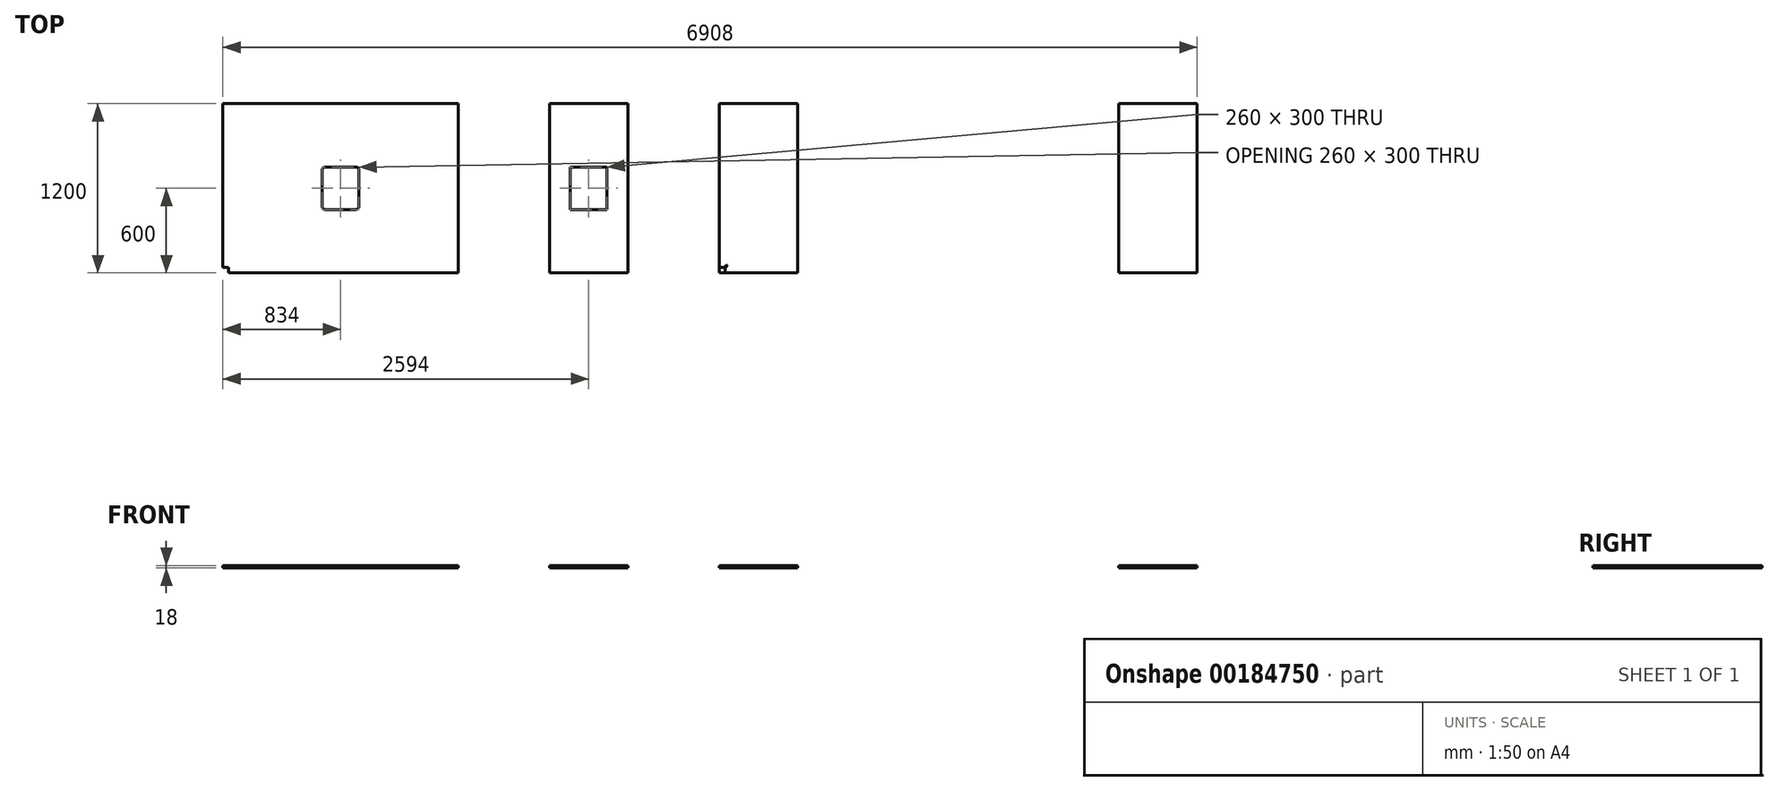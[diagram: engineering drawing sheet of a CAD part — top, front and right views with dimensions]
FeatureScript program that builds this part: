
annotation { "Feature Type Name" : "Feature", "Feature Type Description" : "" }
export const myFeature = defineFeature(function(context is Context, id is Id, definition is map)
    precondition{}
    {
        {
            var Q0;
            Q0=qCreatedBy(makeId("Top.planeOp"),FACE);
            var sketch = newSketch(context, id + "F0", { "sketchPlane" : qUnion([Q0])});
            skLineSegment(sketch, "E0.bottom", {"start": v(834, 600) * mm, "end": v(-834, 600) * mm});
            skLineSegment(sketch, "E0.top", {"start": v(834, -600) * mm, "end": v(-834, -600) * mm});
            skLineSegment(sketch, "E0.left", {"start": v(834, 600) * mm, "end": v(834, -600) * mm});
            skLineSegment(sketch, "E0.right", {"start": v(-834, 600) * mm, "end": v(-834, -600) * mm});
            skPoint(sketch, "E0.middle", {"position": v(0, 0) * mm});
            skLineSegment(sketch, "E1.bottom", {"start": v(130, 150) * mm, "end": v(-130, 150) * mm});
            skLineSegment(sketch, "E1.top", {"start": v(130, -150) * mm, "end": v(-130, -150) * mm});
            skLineSegment(sketch, "E1.left", {"start": v(130, 150) * mm, "end": v(130, -150) * mm});
            skLineSegment(sketch, "E1.right", {"start": v(-130, 150) * mm, "end": v(-130, -150) * mm});
            skLineSegment(sketch, "E2.bottom", {"start": v(-834, -600) * mm, "end": v(-794, -600) * mm});
            skLineSegment(sketch, "E2.top", {"start": v(-834, -560) * mm, "end": v(-794, -560) * mm});
            skLineSegment(sketch, "E2.left", {"start": v(-834, -600) * mm, "end": v(-834, -560) * mm});
            skLineSegment(sketch, "E2.right", {"start": v(-794, -600) * mm, "end": v(-794, -560) * mm});
            skSolve(sketch);
        }
        {
            var Q0;
            Q0=makeQuery(id+"F0.imprint","IMPRINT",FACE,{"disambiguationData":[TD([[makeQuery(id+"F0.imprint","IMPRINT",EDGE,{"derivedFrom":sQuery(id+"F0.wireOp",EDGE,"E0.bottom")}),1.0]])]});
            extrude(context, id + "F1", {"entities" : qUnion([Q0]), "depth" : 18 * mm});
        }
        {
            var Q0;
            Q0=makeQuery(id+"F1.opExtrude","SWEPT_BODY",BODY,{"disambiguationData":[OSD([sQuery(id+"F0.wireOp",EDGE,"E0.bottom"),sQuery(id+"F0.wireOp",EDGE,"E0.top"),sQuery(id+"F0.wireOp",EDGE,"E0.left"),sQuery(id+"F0.wireOp",EDGE,"E0.right"),sQuery(id+"F0.wireOp",EDGE,"E1.bottom"),sQuery(id+"F0.wireOp",EDGE,"E1.top"),sQuery(id+"F0.wireOp",EDGE,"E1.left"),sQuery(id+"F0.wireOp",EDGE,"E1.right"),sQuery(id+"F0.wireOp",EDGE,"E2.top"),sQuery(id+"F0.wireOp",EDGE,"E2.right")])]});
            transform(context, id + "F2", {"entities" : qUnion([Q0]), "transformType" : TransformType.TRANSLATION_3D, "dx" : 1760 * mm, "dy" : 0 * mm, "dz" : 0 * mm, "makeCopy" : true});
        }
        {
            var Q0;
            Q0=makeQuery(id+"F2.opPattern","COPY",BODY,{"derivedFrom":makeQuery(id+"F1.opExtrude","SWEPT_BODY",BODY,{"disambiguationData":[OSD([sQuery(id+"F0.wireOp",EDGE,"E0.bottom"),sQuery(id+"F0.wireOp",EDGE,"E0.top"),sQuery(id+"F0.wireOp",EDGE,"E0.left"),sQuery(id+"F0.wireOp",EDGE,"E0.right"),sQuery(id+"F0.wireOp",EDGE,"E1.bottom"),sQuery(id+"F0.wireOp",EDGE,"E1.top"),sQuery(id+"F0.wireOp",EDGE,"E1.left"),sQuery(id+"F0.wireOp",EDGE,"E1.right"),sQuery(id+"F0.wireOp",EDGE,"E2.top"),sQuery(id+"F0.wireOp",EDGE,"E2.right")])]}),"instanceName":"1"});
            transform(context, id + "F3", {"entities" : qUnion([Q0]), "transformType" : TransformType.TRANSLATION_3D, "dx" : 1760 * mm, "dy" : 0 * mm, "dz" : 0 * mm, "makeCopy" : true});
        }
        {
            var Q0;
            Q0=makeQuery(id+"F3.opPattern","COPY",BODY,{"derivedFrom":makeQuery(id+"F2.opPattern","COPY",BODY,{"derivedFrom":makeQuery(id+"F1.opExtrude","SWEPT_BODY",BODY,{"disambiguationData":[OSD([sQuery(id+"F0.wireOp",EDGE,"E0.bottom"),sQuery(id+"F0.wireOp",EDGE,"E0.top"),sQuery(id+"F0.wireOp",EDGE,"E0.left"),sQuery(id+"F0.wireOp",EDGE,"E0.right"),sQuery(id+"F0.wireOp",EDGE,"E1.bottom"),sQuery(id+"F0.wireOp",EDGE,"E1.top"),sQuery(id+"F0.wireOp",EDGE,"E1.left"),sQuery(id+"F0.wireOp",EDGE,"E1.right"),sQuery(id+"F0.wireOp",EDGE,"E2.top"),sQuery(id+"F0.wireOp",EDGE,"E2.right")])]}),"instanceName":"1"}),"instanceName":"1"});
            transform(context, id + "F4", {"entities" : qUnion([Q0]), "transformType" : TransformType.TRANSLATION_3D, "dx" : 1720 * mm, "dy" : 0 * mm, "dz" : 0 * mm, "makeCopy" : true});
        }
        {
            var Q0;
            Q0=makeQuery(id+"F2.opPattern","COPY",FACE,{"derivedFrom":makeQuery(id+"F1.opExtrude","CAP_FACE",FACE,{"disambiguationData":[OSD([sQuery(id+"F0.wireOp",EDGE,"E0.bottom"),sQuery(id+"F0.wireOp",EDGE,"E0.top"),sQuery(id+"F0.wireOp",EDGE,"E0.left"),sQuery(id+"F0.wireOp",EDGE,"E0.right"),sQuery(id+"F0.wireOp",EDGE,"E1.bottom"),sQuery(id+"F0.wireOp",EDGE,"E1.top"),sQuery(id+"F0.wireOp",EDGE,"E1.left"),sQuery(id+"F0.wireOp",EDGE,"E1.right"),sQuery(id+"F0.wireOp",EDGE,"E2.top"),sQuery(id+"F0.wireOp",EDGE,"E2.right")])],"isStart":false}),"instanceName":"1"});
            var sketch = newSketch(context, id + "F5", { "sketchPlane" : qUnion([Q0])});
            skLineSegment(sketch, "E3.bottom", {"start": v(926, 600) * mm, "end": v(1482, 600) * mm});
            skLineSegment(sketch, "E3.top", {"start": v(926, -600) * mm, "end": v(1482, -600) * mm});
            skLineSegment(sketch, "E3.left", {"start": v(926, 600) * mm, "end": v(926, -600) * mm});
            skLineSegment(sketch, "E3.right", {"start": v(1482, 600) * mm, "end": v(1482, -600) * mm});
            skLineSegment(sketch, "E4.bottom", {"start": v(2594, 600) * mm, "end": v(2038, 600) * mm});
            skLineSegment(sketch, "E4.top", {"start": v(2594, -600) * mm, "end": v(2038, -600) * mm});
            skLineSegment(sketch, "E4.left", {"start": v(2594, 600) * mm, "end": v(2594, -600) * mm});
            skLineSegment(sketch, "E4.right", {"start": v(2038, 600) * mm, "end": v(2038, -600) * mm});
            skSolve(sketch);
        }
        {
            var Q0;
            {var subQ2=sQuery(id+"F5.wireOp",EDGE,"E3.bottom");Q0=makeQuery(id+"F5.imprint","IMPRINT",FACE,{"disambiguationData":[TD([[makeQuery(id+"F5.imprint","IMPRINT",EDGE,{"derivedFrom":subQ2}),1.0]])]});}
            var Q1;
            Q1=makeQuery(id+"F5.imprint","IMPRINT",FACE,{"disambiguationData":[TD([[makeQuery(id+"F5.imprint","IMPRINT",EDGE,{"derivedFrom":sQuery(id+"F5.wireOp",EDGE,"E4.bottom")}),1.0]])]});
            extrude(context, id + "F6", {"entities" : qUnion([Q0, Q1]), "operationType" : NewBodyOperationType.REMOVE, "oppositeDirection" : true, "depth" : 25 * mm});
        }
        {
            var Q0;
            Q0=makeQuery(id+"F3.opPattern","COPY",FACE,{"derivedFrom":makeQuery(id+"F2.opPattern","COPY",FACE,{"derivedFrom":makeQuery(id+"F1.opExtrude","CAP_FACE",FACE,{"disambiguationData":[OSD([sQuery(id+"F0.wireOp",EDGE,"E0.bottom"),sQuery(id+"F0.wireOp",EDGE,"E0.top"),sQuery(id+"F0.wireOp",EDGE,"E0.left"),sQuery(id+"F0.wireOp",EDGE,"E0.right"),sQuery(id+"F0.wireOp",EDGE,"E1.bottom"),sQuery(id+"F0.wireOp",EDGE,"E1.top"),sQuery(id+"F0.wireOp",EDGE,"E1.left"),sQuery(id+"F0.wireOp",EDGE,"E1.right"),sQuery(id+"F0.wireOp",EDGE,"E2.top"),sQuery(id+"F0.wireOp",EDGE,"E2.right")])],"isStart":false}),"instanceName":"1"}),"instanceName":"1"});
            var sketch = newSketch(context, id + "F7", { "sketchPlane" : qUnion([Q0])});
            skLineSegment(sketch, "E5.bottom", {"start": v(4354, 600) * mm, "end": v(3242, 600) * mm});
            skLineSegment(sketch, "E5.top", {"start": v(4354, -600) * mm, "end": v(3242, -600) * mm});
            skLineSegment(sketch, "E5.left", {"start": v(4354, 600) * mm, "end": v(4354, -600) * mm});
            skLineSegment(sketch, "E5.right", {"start": v(3242, 600) * mm, "end": v(3242, -600) * mm});
            skSolve(sketch);
        }
        {
            var Q0;
            Q0=makeQuery(id+"F7.imprint","IMPRINT",FACE,{"disambiguationData":[TD([[makeQuery(id+"F7.imprint","IMPRINT",EDGE,{"derivedFrom":sQuery(id+"F7.wireOp",EDGE,"E5.bottom")}),1.0]])]});
            extrude(context, id + "F8", {"entities" : qUnion([Q0]), "operationType" : NewBodyOperationType.REMOVE, "oppositeDirection" : true, "depth" : 25 * mm});
        }
        {
            var Q0;
            Q0=makeQuery(id+"F4.opPattern","COPY",FACE,{"derivedFrom":makeQuery(id+"F3.opPattern","COPY",FACE,{"derivedFrom":makeQuery(id+"F2.opPattern","COPY",FACE,{"derivedFrom":makeQuery(id+"F1.opExtrude","CAP_FACE",FACE,{"disambiguationData":[OSD([sQuery(id+"F0.wireOp",EDGE,"E0.bottom"),sQuery(id+"F0.wireOp",EDGE,"E0.top"),sQuery(id+"F0.wireOp",EDGE,"E0.left"),sQuery(id+"F0.wireOp",EDGE,"E0.right"),sQuery(id+"F0.wireOp",EDGE,"E1.bottom"),sQuery(id+"F0.wireOp",EDGE,"E1.top"),sQuery(id+"F0.wireOp",EDGE,"E1.left"),sQuery(id+"F0.wireOp",EDGE,"E1.right"),sQuery(id+"F0.wireOp",EDGE,"E2.top"),sQuery(id+"F0.wireOp",EDGE,"E2.right")])],"isStart":false}),"instanceName":"1"}),"instanceName":"1"}),"instanceName":"1"});
            var sketch = newSketch(context, id + "F9", { "sketchPlane" : qUnion([Q0])});
            skLineSegment(sketch, "E6.bottom", {"start": v(4406, 600) * mm, "end": v(5518, 600) * mm});
            skLineSegment(sketch, "E6.top", {"start": v(4406, -600) * mm, "end": v(5518, -600) * mm});
            skLineSegment(sketch, "E6.left", {"start": v(4406, 600) * mm, "end": v(4406, -600) * mm});
            skLineSegment(sketch, "E6.right", {"start": v(5518, 600) * mm, "end": v(5518, -600) * mm});
            skSolve(sketch);
        }
        {
            var Q0;
            {var subQ1=sQuery(id+"F9.wireOp",EDGE,"E6.bottom");Q0=makeQuery(id+"F9.imprint","IMPRINT",FACE,{"disambiguationData":[TD([[makeQuery(id+"F9.imprint","IMPRINT",EDGE,{"derivedFrom":subQ1}),1.0]])]});}
            extrude(context, id + "F10", {"entities" : qUnion([Q0]), "operationType" : NewBodyOperationType.REMOVE, "oppositeDirection" : true, "depth" : 25 * mm});
        }
        {
            var Q0;
            Q0=makeQuery(id+"F1.opExtrude","SWEPT_EDGE",EDGE,{"disambiguationData":[OSD([sQuery(id+"F0.wireOp",EDGE,"E1.bottom"),sQuery(id+"F0.wireOp",EDGE,"E1.right")])]});
            var Q1;
            Q1=makeQuery(id+"F1.opExtrude","SWEPT_EDGE",EDGE,{"disambiguationData":[OSD([sQuery(id+"F0.wireOp",EDGE,"E1.top"),sQuery(id+"F0.wireOp",EDGE,"E1.right")])]});
            var Q2;
            Q2=makeQuery(id+"F1.opExtrude","SWEPT_EDGE",EDGE,{"disambiguationData":[OSD([sQuery(id+"F0.wireOp",EDGE,"E1.top"),sQuery(id+"F0.wireOp",EDGE,"E1.left")])]});
            var Q3;
            Q3=makeQuery(id+"F1.opExtrude","SWEPT_EDGE",EDGE,{"disambiguationData":[OSD([sQuery(id+"F0.wireOp",EDGE,"E1.bottom"),sQuery(id+"F0.wireOp",EDGE,"E1.left")])]});
            fillet(context, id + "F11", {"entities" : qUnion([Q0, Q1, Q2, Q3]), "radius" : 20 * mm, "tangentPropagation" : true, "allowEdgeOverflow" : false});
        }
        {
            var Q0;
            Q0=makeQuery(id+"F3.opPattern","COPY",FACE,{"derivedFrom":makeQuery(id+"F2.opPattern","COPY",FACE,{"derivedFrom":makeQuery(id+"F1.opExtrude","CAP_FACE",FACE,{"disambiguationData":[OSD([sQuery(id+"F0.wireOp",EDGE,"E0.bottom"),sQuery(id+"F0.wireOp",EDGE,"E0.top"),sQuery(id+"F0.wireOp",EDGE,"E0.left"),sQuery(id+"F0.wireOp",EDGE,"E0.right"),sQuery(id+"F0.wireOp",EDGE,"E1.bottom"),sQuery(id+"F0.wireOp",EDGE,"E1.top"),sQuery(id+"F0.wireOp",EDGE,"E1.left"),sQuery(id+"F0.wireOp",EDGE,"E1.right"),sQuery(id+"F0.wireOp",EDGE,"E2.top"),sQuery(id+"F0.wireOp",EDGE,"E2.right")])],"isStart":false}),"instanceName":"1"}),"instanceName":"1"});
            var sketch = newSketch(context, id + "F12", { "sketchPlane" : qUnion([Q0])});
            skLineSegment(sketch, "E7.bottom", {"start": v(2686, -560) * mm, "end": v(2726, -560) * mm});
            skLineSegment(sketch, "E7.top", {"start": v(2686, -600) * mm, "end": v(2726, -600) * mm});
            skLineSegment(sketch, "E7.left", {"start": v(2686, -560) * mm, "end": v(2686, -600) * mm});
            skLineSegment(sketch, "E7.right", {"start": v(2726, -560) * mm, "end": v(2726, -600) * mm});
            skLineSegment(sketch, "E8", {"start": v(2686, -600) * mm, "end": v(2738.02, -547.98) * mm, "construction": true});
            skCircle(sketch, "E9", {"center": v(2738.02, -547.98) * mm, "radius": 3 * mm, "construction": true});
            skLineSegment(sketch, "E10", {"start": v(2735.9, -545.86) * mm, "end": v(2721.76, -560) * mm});
            skLineSegment(sketch, "E11", {"start": v(2740.14, -550.1) * mm, "end": v(2726, -564.24) * mm});
            skArc(sketch, "E12", {"start": v(2740.14, -550.1) * mm, "mid": v(2740.14, -545.86) * mm, "end": v(2735.9, -545.86) * mm});
            skSolve(sketch);
        }
        {
            var Q0;
            {var subQ5=sQuery(id+"F12.wireOp",EDGE,"E7.top");Q0=makeQuery(id+"F12.imprint","IMPRINT",FACE,{"disambiguationData":[TD([[makeQuery(id+"F12.imprint","IMPRINT",EDGE,{"derivedFrom":subQ5}),1.0]])]});}
            var Q1;
            {var subQ0=sQuery(id+"F12.wireOp",EDGE,"E10");Q1=makeQuery(id+"F12.imprint","IMPRINT",FACE,{"disambiguationData":[TD([[makeQuery(id+"F12.imprint","IMPRINT",EDGE,{"derivedFrom":subQ0}),1.0]])]});}
            var Q2;
            Q2=makeQuery(id+"F3.opPattern","COPY",FACE,{"derivedFrom":makeQuery(id+"F2.opPattern","COPY",FACE,{"derivedFrom":makeQuery(id+"F1.opExtrude","CAP_FACE",FACE,{"disambiguationData":[OSD([sQuery(id+"F0.wireOp",EDGE,"E0.bottom"),sQuery(id+"F0.wireOp",EDGE,"E0.top"),sQuery(id+"F0.wireOp",EDGE,"E0.left"),sQuery(id+"F0.wireOp",EDGE,"E0.right"),sQuery(id+"F0.wireOp",EDGE,"E1.bottom"),sQuery(id+"F0.wireOp",EDGE,"E1.top"),sQuery(id+"F0.wireOp",EDGE,"E1.left"),sQuery(id+"F0.wireOp",EDGE,"E1.right"),sQuery(id+"F0.wireOp",EDGE,"E2.top"),sQuery(id+"F0.wireOp",EDGE,"E2.right")])],"isStart":true}),"instanceName":"1"}),"instanceName":"1"});
            extrude(context, id + "F13", {"entities" : qUnion([Q0, Q1]), "endBound" : BoundingType.UP_TO_SURFACE, "oppositeDirection" : true, "endBoundEntityFace" : qUnion([Q2]), "depth" : 25 * mm});
        }
        {
            var Q0;
            Q0=makeQuery(id+"F13.opExtrude","SWEPT_BODY",BODY,{"disambiguationData":[OSD([sQuery(id+"F12.wireOp",EDGE,"E7.bottom"),sQuery(id+"F12.wireOp",EDGE,"E7.top"),sQuery(id+"F12.wireOp",EDGE,"E7.left"),sQuery(id+"F12.wireOp",EDGE,"E7.right"),sQuery(id+"F12.wireOp",EDGE,"E10"),sQuery(id+"F12.wireOp",EDGE,"E11"),sQuery(id+"F12.wireOp",EDGE,"E12")])]});
            var Q1;
            Q1=makeQuery(id+"F3.opPattern","COPY",BODY,{"derivedFrom":makeQuery(id+"F2.opPattern","COPY",BODY,{"derivedFrom":makeQuery(id+"F1.opExtrude","SWEPT_BODY",BODY,{"disambiguationData":[OSD([sQuery(id+"F0.wireOp",EDGE,"E0.bottom"),sQuery(id+"F0.wireOp",EDGE,"E0.top"),sQuery(id+"F0.wireOp",EDGE,"E0.left"),sQuery(id+"F0.wireOp",EDGE,"E0.right"),sQuery(id+"F0.wireOp",EDGE,"E1.bottom"),sQuery(id+"F0.wireOp",EDGE,"E1.top"),sQuery(id+"F0.wireOp",EDGE,"E1.left"),sQuery(id+"F0.wireOp",EDGE,"E1.right"),sQuery(id+"F0.wireOp",EDGE,"E2.top"),sQuery(id+"F0.wireOp",EDGE,"E2.right")])]}),"instanceName":"1"}),"instanceName":"1"});
            booleanBodies(context, id + "F14", {"operationType" : BooleanOperationType.SUBTRACTION, "tools" : qUnion([Q0]), "targets" : qUnion([Q1])});
        }
        {
            var Q0;
            {var subQ5=sQuery(id+"F12.wireOp",EDGE,"E7.top");Q0=makeQuery(id+"F12.imprint","IMPRINT",FACE,{"disambiguationData":[TD([[makeQuery(id+"F12.imprint","IMPRINT",EDGE,{"derivedFrom":subQ5}),1.0]])]});}
            var Q1;
            {var subQ0=sQuery(id+"F12.wireOp",EDGE,"E10");Q1=makeQuery(id+"F12.imprint","IMPRINT",FACE,{"disambiguationData":[TD([[makeQuery(id+"F12.imprint","IMPRINT",EDGE,{"derivedFrom":subQ0}),1.0]])]});}
            var Q2;
            Q2=makeQuery(id+"F3.opPattern","COPY",FACE,{"derivedFrom":makeQuery(id+"F2.opPattern","COPY",FACE,{"derivedFrom":makeQuery(id+"F1.opExtrude","CAP_FACE",FACE,{"disambiguationData":[OSD([sQuery(id+"F0.wireOp",EDGE,"E0.bottom"),sQuery(id+"F0.wireOp",EDGE,"E0.top"),sQuery(id+"F0.wireOp",EDGE,"E0.left"),sQuery(id+"F0.wireOp",EDGE,"E0.right"),sQuery(id+"F0.wireOp",EDGE,"E1.bottom"),sQuery(id+"F0.wireOp",EDGE,"E1.top"),sQuery(id+"F0.wireOp",EDGE,"E1.left"),sQuery(id+"F0.wireOp",EDGE,"E1.right"),sQuery(id+"F0.wireOp",EDGE,"E2.top"),sQuery(id+"F0.wireOp",EDGE,"E2.right")])],"isStart":true}),"instanceName":"1"}),"instanceName":"1"});
            extrude(context, id + "F15", {"entities" : qUnion([Q0, Q1]), "endBound" : BoundingType.UP_TO_SURFACE, "oppositeDirection" : true, "endBoundEntityFace" : qUnion([Q2]), "depth" : 25 * mm});
        }
    });
